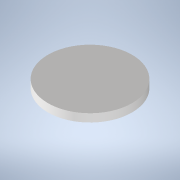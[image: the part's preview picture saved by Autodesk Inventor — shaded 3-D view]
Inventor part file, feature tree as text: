
AUTODESK INVENTOR PART (.ipt)
format: ipt  version: 2022 (Build 260153000, 153)  size: 113,152 bytes
history: native  units: mm
features: extrude x3, sketch x3
ambient origin geometry x8: Origin, YZ Plane, XZ Plane, XY Plane, X Axis, Y Axis, Z Axis, Center Point
bodies: Solid1 (feature_tree)
feature tree (6):
  extrude  "Extrusion1"  Depth=8.75mm
  extrude  "Extrusion2"  Depth=0.6mm TaperAngle=0.0deg
  extrude  "Extrusion3"  Depth=2.4mm
  sketch  "Sketch1"  dims[d0=6.0mm d1=8.75mm]
  sketch  "Sketch2"  dims[d2=2.7mm d3=0.0mm d4=0.6mm d5=0.0mm]
  sketch  "Sketch3"  dims[d7=2.4mm d8=0.0mm d9=25.0mm]
